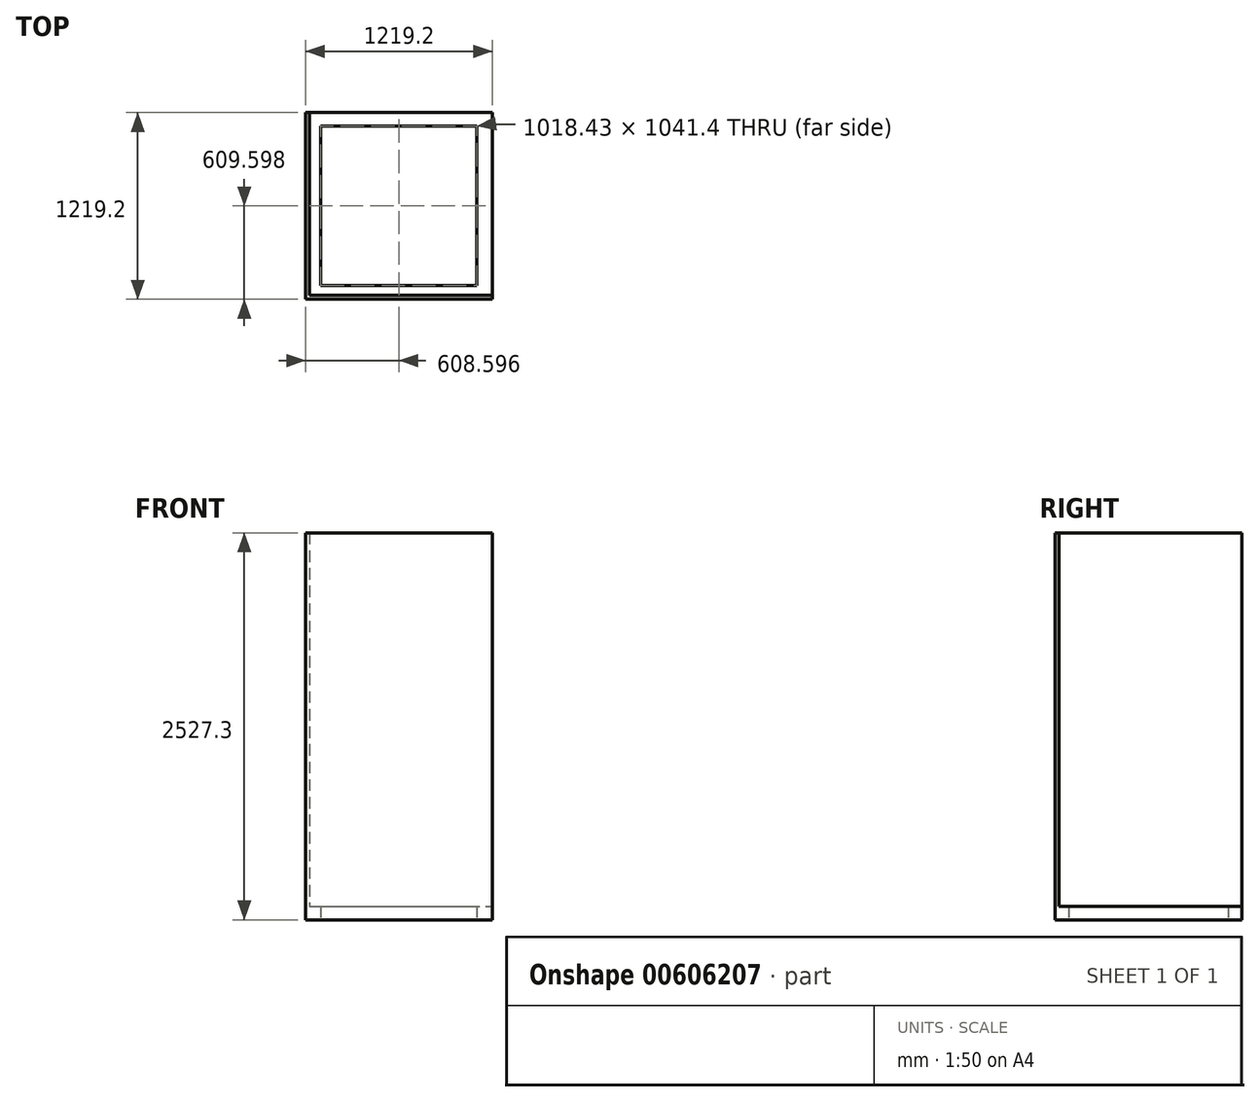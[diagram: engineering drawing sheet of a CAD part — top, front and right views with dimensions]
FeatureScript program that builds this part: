
annotation { "Feature Type Name" : "Feature", "Feature Type Description" : "" }
export const myFeature = defineFeature(function(context is Context, id is Id, definition is map)
    precondition{}
    {
        {
            var Q0;
            Q0=qCreatedBy(makeId("Top.planeOp"),FACE);
            var sketch = newSketch(context, id + "F0", { "sketchPlane" : qUnion([Q0])});
            skLineSegment(sketch, "E0.bottom", {"start": v(-541.55, 565.44) * mm, "end": v(677.65, 565.44) * mm});
            skLineSegment(sketch, "E0.top", {"start": v(-541.55, -653.76) * mm, "end": v(677.65, -653.76) * mm});
            skLineSegment(sketch, "E0.left", {"start": v(-541.55, 565.44) * mm, "end": v(-541.55, -653.76) * mm});
            skLineSegment(sketch, "E0.right", {"start": v(677.65, 565.44) * mm, "end": v(677.65, -653.76) * mm});
            skLineSegment(sketch, "E1.bottom", {"start": v(-442.17, 476.54) * mm, "end": v(576.26, 476.54) * mm});
            skLineSegment(sketch, "E1.top", {"start": v(-442.17, -564.86) * mm, "end": v(576.26, -564.86) * mm});
            skLineSegment(sketch, "E1.left", {"start": v(-442.17, 476.54) * mm, "end": v(-442.17, -564.86) * mm});
            skLineSegment(sketch, "E1.right", {"start": v(576.26, 476.54) * mm, "end": v(576.26, -564.86) * mm});
            skSolve(sketch);
        }
        {
            var Q0;
            Q0 = qSketchRegion(id + "F0", true);
            extrude(context, id + "F1", {"entities" : qUnion([Q0]), "depth" : 88.9 * mm, "offsetDistance" : 25.4 * mm});
        }
        {
            var Q0;
            Q0=makeQuery(id+"F1.opExtrude","CAP_FACE",FACE,{"disambiguationData":[OSD([sQuery(id+"F0.wireOp",EDGE,"E0.bottom"),sQuery(id+"F0.wireOp",EDGE,"E0.top"),sQuery(id+"F0.wireOp",EDGE,"E0.left"),sQuery(id+"F0.wireOp",EDGE,"E0.right"),sQuery(id+"F0.wireOp",EDGE,"E1.bottom"),sQuery(id+"F0.wireOp",EDGE,"E1.top"),sQuery(id+"F0.wireOp",EDGE,"E1.left"),sQuery(id+"F0.wireOp",EDGE,"E1.right")])],"isStart":false});
            var sketch = newSketch(context, id + "F2", { "sketchPlane" : qUnion([Q0])});
            skLineSegment(sketch, "E2.bottom", {"start": v(677.65, -653.76) * mm, "end": v(-541.55, -653.76) * mm});
            skLineSegment(sketch, "E2.top", {"start": v(677.65, -628.36) * mm, "end": v(-516.15, -628.36) * mm});
            skLineSegment(sketch, "E2.left", {"start": v(677.65, -653.76) * mm, "end": v(677.65, -628.36) * mm});
            skLineSegment(sketch, "E2.right", {"start": v(-541.55, -653.76) * mm, "end": v(-541.55, -628.36) * mm});
            skLineSegment(sketch, "E3.top", {"start": v(-541.55, 565.44) * mm, "end": v(-516.15, 565.44) * mm});
            skLineSegment(sketch, "E3.left", {"start": v(-541.55, -628.36) * mm, "end": v(-541.55, 565.44) * mm});
            skLineSegment(sketch, "E3.right", {"start": v(-516.15, -628.36) * mm, "end": v(-516.15, 565.44) * mm});
            skSolve(sketch);
        }
        {
            var Q0;
            Q0=makeQuery(id+"F2.imprint","IMPRINT",FACE,{"disambiguationData":[TD([[makeQuery(id+"F2.imprint","IMPRINT",EDGE,{"derivedFrom":sQuery(id+"F2.wireOp",EDGE,"E2.bottom")}),1.0]])]});
            extrude(context, id + "F3", {"entities" : qUnion([Q0]), "operationType" : NewBodyOperationType.ADD, "depth" : 2438.4 * mm, "offsetDistance" : 25.4 * mm});
        }
    });
